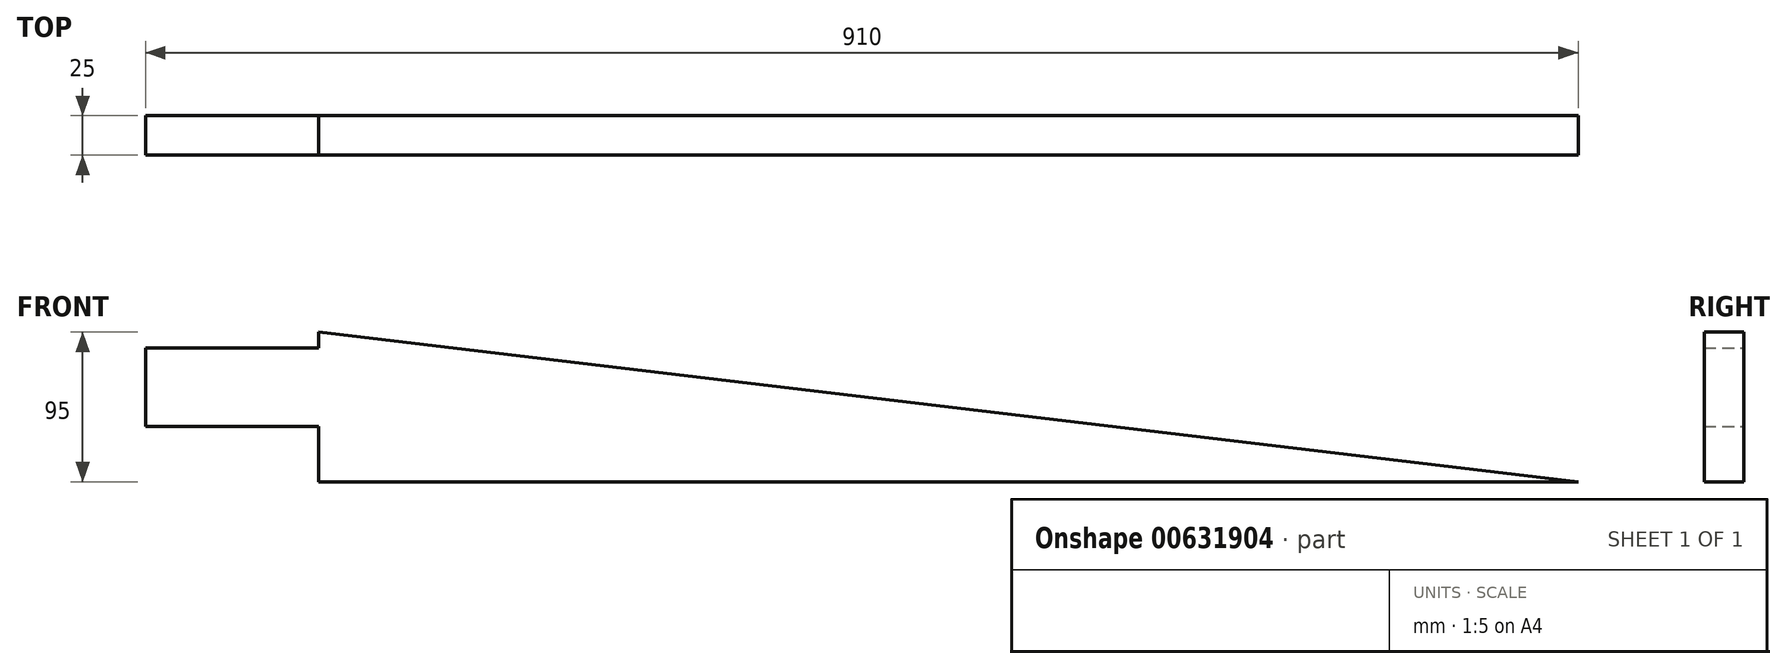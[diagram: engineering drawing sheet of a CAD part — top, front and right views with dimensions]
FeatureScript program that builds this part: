
annotation { "Feature Type Name" : "Feature", "Feature Type Description" : "" }
export const myFeature = defineFeature(function(context is Context, id is Id, definition is map)
    precondition{}
    {
        {
            var Q0;
            Q0=qCreatedBy(makeId("Front.planeOp"),FACE);
            var sketch = newSketch(context, id + "F0", { "sketchPlane" : qUnion([Q0])});
            skLineSegment(sketch, "E0", {"start": v(-256.01, 89.34) * mm, "end": v(-256.01, 39.34) * mm});
            skLineSegment(sketch, "E1", {"start": v(-256.01, 39.34) * mm, "end": v(-146.01, 39.34) * mm});
            skLineSegment(sketch, "E2", {"start": v(-146.01, 39.34) * mm, "end": v(-146.01, 4.34) * mm});
            skLineSegment(sketch, "E3", {"start": v(-146.01, 4.34) * mm, "end": v(653.99, 4.34) * mm});
            skLineSegment(sketch, "E4", {"start": v(653.99, 4.34) * mm, "end": v(-146.01, 99.34) * mm});
            skLineSegment(sketch, "E5", {"start": v(-146.01, 99.34) * mm, "end": v(-146.01, 89.34) * mm});
            skLineSegment(sketch, "E6", {"start": v(-146.01, 89.34) * mm, "end": v(-256.01, 89.34) * mm});
            skSolve(sketch);
        }
        {
            var Q0;
            Q0=makeQuery(id+"F0.imprint","IMPRINT",FACE,{"disambiguationData":[TD([[makeQuery(id+"F0.imprint","IMPRINT",EDGE,{"derivedFrom":sQuery(id+"F0.wireOp",EDGE,"E0")}),1.0]])]});
            extrude(context, id + "F1", {"entities" : qUnion([Q0]), "depth" : 25 * mm, "offsetDistance" : 25 * mm});
        }
    });
